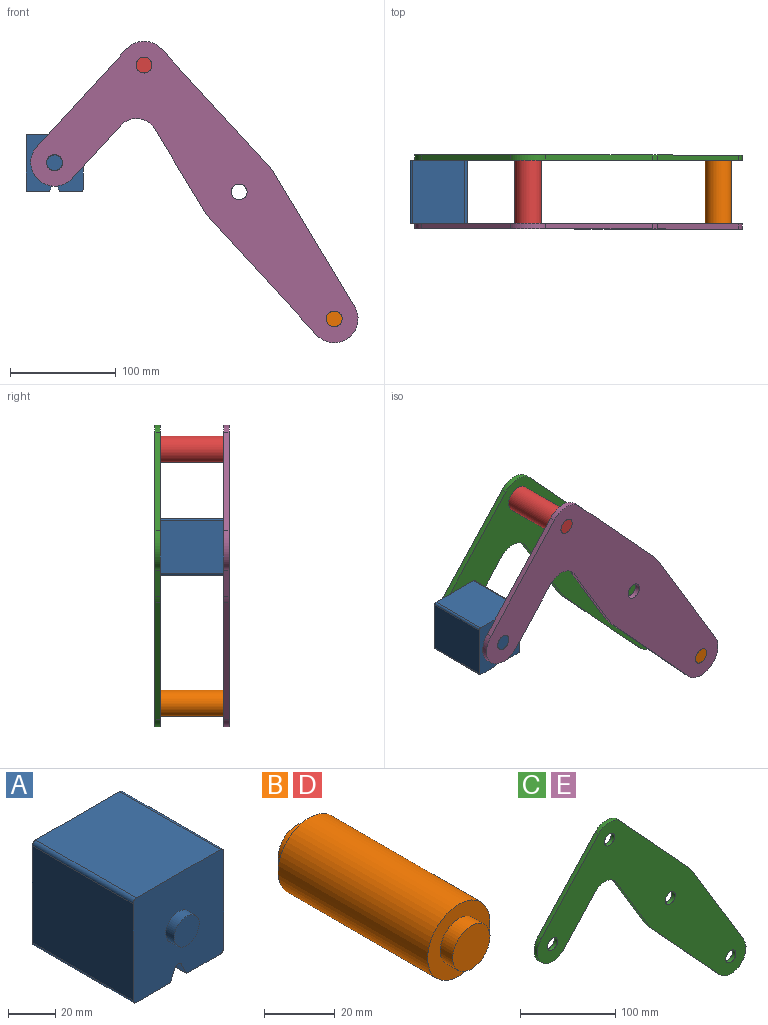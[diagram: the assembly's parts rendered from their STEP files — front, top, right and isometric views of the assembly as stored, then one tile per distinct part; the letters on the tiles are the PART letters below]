
ASSEMBLY  parts=5 mates=3
PART A: 18 faces, bbox 54x70x54 mm
  f0: plane 60x50.01mm, normal (0,0,1), area 3000.4mm2, adj f4,f10,f13,f14
  f1: plane 60x50.01mm, normal (-1,0,0), area 3000.4mm2, adj f4,f10,f14,f15
  f2: plane 60x20mm, normal (0,0,-1), area 1200.2mm2, adj f3,f4,f10,f15
  f3: plane 60x6.42mm, normal (0.89,0,-0.45), area 430.8mm2, adj f2,f4,f10,f16
  f4: plane 54.01x54.01mm, normal (0,-1,0), area 2690.1mm2, adj f0,f1,f2,f3,f5,f6,f7,f9
  f5: plane 60x50.01mm, normal (1,0,0), area 3000.4mm2, adj f4,f10,f13,f17
  f6: plane 60x6.42mm, normal (-0.89,0,-0.45), area 430.8mm2, adj f4,f7,f10,f16
  f7: plane 60x20mm, normal (0,0,-1), area 1200.2mm2, adj f4,f6,f10,f17
  f8: plane 15x15mm, normal (0,-1,0), area 176.7mm2, adj f9
  f9: cylinder r=7.5mm len=15mm, axis (0,1,0), area 235.6mm2, adj f4,f8
  f10: plane 54.01x54.01mm, normal (0,1,0), area 2690.1mm2, adj f0,f1,f2,f3,f5,f6,f7,f12
  f11: plane 15x15mm, normal (0,1,0), area 176.7mm2, adj f12
  f12: cylinder r=7.5mm len=15mm, axis (0,-1,0), area 235.6mm2, adj f10,f11
  f13: cylinder r=2mm len=60mm, axis (0,-1,0), area 188.5mm2, adj f0,f4,f5,f10
  f14: cylinder r=2mm len=60mm, axis (0,1,0), area 188.5mm2, adj f0,f1,f4,f10
  f15: cylinder r=2mm len=60mm, axis (0,-1,0), area 188.5mm2, adj f1,f2,f4,f10
  f16: cylinder r=2mm len=60mm, axis (0,-1,0), area 265.7mm2, adj f3,f4,f6,f10
  f17: cylinder r=2mm len=60mm, axis (0,1,0), area 188.5mm2, adj f4,f5,f7,f10
PART B: 7 faces, bbox 25x70x25 mm
  f0: cylinder r=12.5mm len=60mm, axis (0,-1,0), area 4712.4mm2, adj f2,f5
  f1: cylinder r=7.5mm len=15mm, axis (0,1,0), area 235.6mm2, adj f2,f3
  f2: plane 25x25mm, normal (0,-1,0), area 314.2mm2, adj f0,f1
  f3: plane 15x15mm, normal (0,-1,0), area 176.7mm2, adj f1
  f4: cylinder r=7.5mm len=15mm, axis (0,-1,0), area 235.6mm2, adj f5,f6
  f5: plane 25x25mm, normal (0,1,0), area 314.2mm2, adj f0,f4
  f6: plane 15x15mm, normal (0,1,0), area 176.7mm2, adj f4
PART C: 18 faces, bbox 309.5x5x285.1 mm
  f0: cylinder r=22.5mm len=39.07mm, axis (0,1,0), area 353.4mm2, adj f1,f13,f16,f17
  f1: plane 50.28x46.21mm, normal (0.74,0,-0.68), area 341.4mm2, adj f0,f2,f16,f17
  f2: cylinder r=20mm len=31.85mm, axis (0,1,0), area 185.5mm2, adj f1,f3,f16,f17
  f3: plane 79.23x47.81mm, normal (-0.86,0,-0.52), area 462.7mm2, adj f2,f4,f16,f17
  f4: cylinder r=37.5mm len=6mm, axis (0,1,0), area 37.6mm2, adj f3,f5,f16,f17
  f5: plane 109.88x101mm, normal (-0.74,0,-0.68), area 746.2mm2, adj f4,f6,f16,f17
  f6: cylinder r=22.5mm len=39.07mm, axis (0,1,0), area 330.9mm2, adj f5,f7,f16,f17
  f7: plane 127.78x77.11mm, normal (0.86,0,0.52), area 746.2mm2, adj f6,f8,f16,f17
  f8: cylinder r=37.5mm len=6mm, axis (0,1,0), area 37.6mm2, adj f7,f9,f16,f17
  f9: plane 109.88x101mm, normal (0.74,0,0.68), area 746.2mm2, adj f8,f10,f16,f17
  f10: cylinder r=22.5mm len=33.13mm, axis (0,1,0), area 186.2mm2, adj f9,f13,f16,f17
  f11: cylinder r=7.5mm len=15mm, axis (0,1,0), area 235.6mm2, adj f16,f17
  f12: cylinder r=7.5mm len=15mm, axis (0,1,0), area 235.6mm2, adj f16,f17
  f13: plane 92.03x84.59mm, normal (-0.74,0,0.68), area 625mm2, adj f0,f10,f16,f17
  f14: cylinder r=7.5mm len=15mm, axis (0,1,0), area 235.6mm2, adj f16,f17
  f15: cylinder r=7.5mm len=15mm, axis (0,1,0), area 235.6mm2, adj f16,f17
  f16: plane 309.5x285.07mm, normal (0,-1,0), area 24555.4mm2, adj f0,f1,f2,f3,f4,f5,f6,f7
  f17: plane 309.5x285.07mm, normal (0,1,0), area 24555.4mm2, adj f0,f1,f2,f3,f4,f5,f6,f7
PART D: same geometry as B
PART E: same geometry as C
PLACE A t=(0,-30,-0.41)mm
PLACE B t=(179.91,-30,-240.07)mm
PLACE C t=(0,35,0)mm
PLACE D t=(0,-30,0)mm
PLACE E t=(0,-30,0)mm fixed
MATE revolute A.f4 <-> E.f0  axis (0,-1,0) through (-174.54,-30,28)mm
MATE fastened B.f0 <-> E.f6  axis (0,1,0) through (89.96,-30,-120.03)mm
MATE fastened C.f10 <-> D.f0  axis (0,-1,0) through (-89.96,30,120.03)mm
